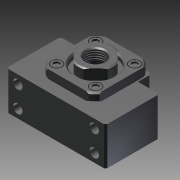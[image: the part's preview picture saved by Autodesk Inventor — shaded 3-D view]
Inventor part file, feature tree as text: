
AUTODESK INVENTOR PART (.ipt)
format: ipt  version: 2016 (Build 200138000, 138)  size: 390,144 bytes
history: native  units: mm
features: sketch x26, other x14, revolve x12, extrude x9, hole x5, pattern_linear x3, thread x1
ambient origin geometry x8: Origin, YZ Plane, XZ Plane, XY Plane, X Axis, Y Axis, Z Axis, Center Point
bodies: Solid1 (feature_tree)
feature tree (70):
  extrude  "Extrusion1"  Depth=2.5mm TaperAngle=0.0deg
  hole  "Hole1"  [1 undecoded]
  hole  "Hole2"  [1 undecoded]
  hole  "Hole3"  [1 undecoded]
  hole  "Hole4"  [1 undecoded]
  extrude  "Extrusion2"  Depth=20.0mm
  revolve  "Revolution1"  [1 undecoded]
  extrude  "Extrusion3"  Depth=20.0mm
  extrude  "Extrusion4"  TaperAngle=360.0deg  [1 undecoded]
  revolve  "Revolution2"  Angle=360.0deg
  hole  "Hole5"  [1 undecoded]
  revolve  "Revolution3"  Angle=360.0deg
  thread  "Thread1"  [1 undecoded]
  revolve  "Revolution4"  [1 undecoded]
  revolve  "Revolution5"  [1 undecoded]
  pattern_linear  "Rectangular Pattern1"  [2 undecoded]
  revolve  "Revolution6"  [1 undecoded]
  pattern_linear  "Rectangular Pattern2"  [2 undecoded]
  extrude  "Extrusion5"  [1 undecoded]
  pattern_linear  "Rectangular Pattern3"  [2 undecoded]
  revolve  "Revolution7"  [1 undecoded]
  revolve  "Revolution8"  [1 undecoded]
  extrude  "Extrusion6"  [1 undecoded]
  revolve  "Revolution9"  [1 undecoded]
  revolve  "Revolution10"  [1 undecoded]
  extrude  "Extrusion7"  [1 undecoded]
  extrude  "Extrusion8"  [1 undecoded]
  revolve  "Revolution11"  [1 undecoded]
  revolve  "Revolution12"  [1 undecoded]
  extrude  "Extrusion9"  [1 undecoded]
  other  "unit_XY"
  other  "unit_YZ"
  other  "unit_ZX"
  other  "unit_X"
  other  "unit_Y"
  other  "unit_Z"
  other  "unit_Center"
  other  "unit_collar_XY"
  other  "unit_collar_YZ"
  other  "unit_collar_ZX"
  other  "unit_collar_X"
  other  "unit_collar_Y"
  other  "unit_collar_Z"
  other  "unit_collar_Center"
  sketch  "Sketch_1"  dims[d0=27.0mm d1=0.0mm]
  sketch  "Sketch2"  dims[d2=6.6mm d3=6.0mm d4=11.0mm d5=6.5mm d6=90.0deg d7=38.0mm d8=0.0mm]
  sketch  "Sketch3"  dims[d9=6.6mm d10=6.0mm d11=11.0mm d12=6.5mm d13=90.0deg d14=38.0mm d15=0.0mm]
  sketch  "Sketch4"  dims[d16=6.6mm d17=6.0mm d18=11.0mm d19=6.5mm d20=90.0deg d21=38.0mm d22=0.0mm]
  sketch  "Sketch5"  dims[d23=6.6mm d24=6.0mm d25=11.0mm d26=6.5mm d27=90.0deg d28=38.0mm d29=0.0mm d30=2.5mm d31=0.0mm]
  sketch  "Sketch_10"  dims[d32=360.0deg d33=8.5mm d34=0.0mm]
  sketch  "Sketch_13"  dims[d49=360.0deg d50=20.0mm d52=27.577164mm d53=20.0mm d55=27.577164mm]
  sketch  "Sketch_11"  dims[d35=3.5mm d36=0.0mm d37=360.0deg]
  sketch  "Sketch_12"  dims[d46=6.876mm d47=0.0mm d48=360.0deg]
  sketch  "Sketch_14"  dims[d56=360.0deg d57=20.0mm d59=27.577164mm d60=20.0mm d62=27.577164mm]
  sketch  "Sketch11"  dims[d38=15.0mm d39=6.0mm d40=19.5mm d41=6.0mm d42=90.0deg d43=30.0mm d44=0.0mm d45=360.0deg]
  sketch  "Sketch_16"  dims[d63=1.2mm d64=0.0mm d65=20.0mm d67=27.577164mm d68=20.0mm d70=27.577164mm]
  sketch  "Sketch_17"  dims[d71=360.0deg d72=360.0deg]
  sketch  "Sketch_18"  dims[d73=1.2mm d74=0.0mm d75=360.0deg]
  sketch  "Sketch_20"  dims[d76=360.0deg d77=16.0mm d78=0.0mm]
  sketch  "Sketch_22"  dims[d79=6.0mm d80=0.0mm d81=360.0deg d82=360.0deg]
  sketch  "Sketch_24"  dims[d83=0.01mm d84=0.0mm d85=0.0mm d86=0.0mm]
  sketch  "Sketch_25"
  sketch  "Sketch_26"
  sketch  "Sketch_28"
  sketch  "Sketch_29"
  sketch  "Sketch_33"
  sketch  "Sketch_27"
  sketch  "Sketch_30"
  sketch  "Sketch_31"
  sketch  "Sketch_32"
note: 28 required parameter values undecoded (feature->parameter linkage not recoverable at this tier; creation-order binding heuristic only, values carry confidence <= 0.55)